# Revit family: HC_Boiler_Condensate Flow_MEPcontent_De Dietrich Thermique_C230 Evo_INT-EN
name_source: partatom
category: Mechanical Equipment
units: mm (PartAtom-declared; Revit-internal decimal feet)

## family parameters
Always vertical = Yes
Cut with Voids When Loaded = No
OmniClass Number = 23.75.10.11.14
OmniClass Title = Hot Water Heat Generators
Part Type = Normal
Room Calculation Point = No
Round Connector Dimension = Use Diameter
Shared = No
Work Plane-Based = No

## types (4) — shared parameters
Article Description = High-efficiency standing gas boiler
Base Family Version = 23.05
Black = Color RGB 040-040-040
Blue = Color RGB 000-112-208
Content Supplier URL = www.MEPcontent.com
Custom = No
Dark Grey = Color RGB 040-040-040
Depth = 450 mm  [stored 1.47638 ft]
Description = High-efficiency standing gas boiler
Drain Diameter = 32 mm  [stored 0.104987 ft]
EMCS Version = 4.0
ETIM Article Class = EC010231
Family Version = 23.05
Flue Gas diameter = 150 mm  [stored 0.492126 ft]
Front Clearance = 600 mm
Grey = Color RGB 128-128-128
Height = 1368 mm  [stored 4.48819 ft]
Hertz = 50 Hz
Hydronic Return Nominal Diameter = 42.4 mm  [stored 0.139108 ft]
Hydronic Supply Nominal Diameter = 42.4 mm  [stored 0.139108 ft]
IFCExportAs = IfcBoiler
IFCExportType = NOTDEFINED
Left Clearance = 50 mm  [stored 0.164042 ft]
Light Grey = Color RGB 176-176-176
MEPcontent Class = BOILER_CONDENSATE_FLOW
Manufacturer = De Dietrich Thermique
Manufacturer URL = https://www.dedietrich-thermique.fr
Maximum Operating Pressure = 6.0 bar
Maximum Supply Temperature = 110 °C
Maximum Supply Temperature (Operating Temperature) = 90 °C
Minimum Operating Pressure = 0.8 bar
Phase = 1
Product Line = De Dietrich Thermique
Red = Color RGB 176-000-000
Revit Version = 2020
Right Clearance = 250 mm  [stored 0.82021 ft]
Supply Air Diameter = 150 mm  [stored 0.492126 ft]
Top Clearance = 382 mm  [stored 1.25328 ft]
URL = https://mep.trimble.com
Use Nominal Diameter = Yes
Voltage = 230 V
White = Color RGB 192-192-192
Width = 1190 mm  [stored 3.9042 ft]
Yellow = Color RGB 229-229-000
zero-valued in all types: Default Elevation

## per-type parameters (varying)
| type | B | B2 | Central Heating Connectors Lenght | Hydronic Return and Supply Fiting Visibility | Nominal Power 50-30 °C (kW) | Nominal Power 80-60 °C (kW) |
| 85 | 31.8 mm  [stored 0.104331 ft] | 42.4 mm  [stored 0.139108 ft] | 31 mm  [stored 0.101706 ft] | No | 20 - 93 | 18 - 87 |
| 130 | 31.8 mm  [stored 0.104331 ft] | 42.4 mm  [stored 0.139108 ft] | 31 mm  [stored 0.101706 ft] | No | 24 - 129 | 22 - 120 |
| 170 | 31.8 mm  [stored 0.104331 ft] | 42.4 mm  [stored 0.139108 ft] | 31 mm  [stored 0.101706 ft] | No | 33 - 179 | 29 - 166 |
| 210 | 38.1 mm  [stored 0.125 ft] | 48.3 mm  [stored 0.158465 ft] | 16 mm  [stored 0.0524934 ft] | Yes | 44 - 217 | 39 - 200 |

note: column(s) folded — value = type name in every type: Article Type, Model

note: [stored X ft] marks values corroborated as IEEE doubles in the binary element streams (Revit-internal decimal feet)

## geometry (parser evidence)
native form markers: Sweep x8
no freeform markers — native parametric forms only
